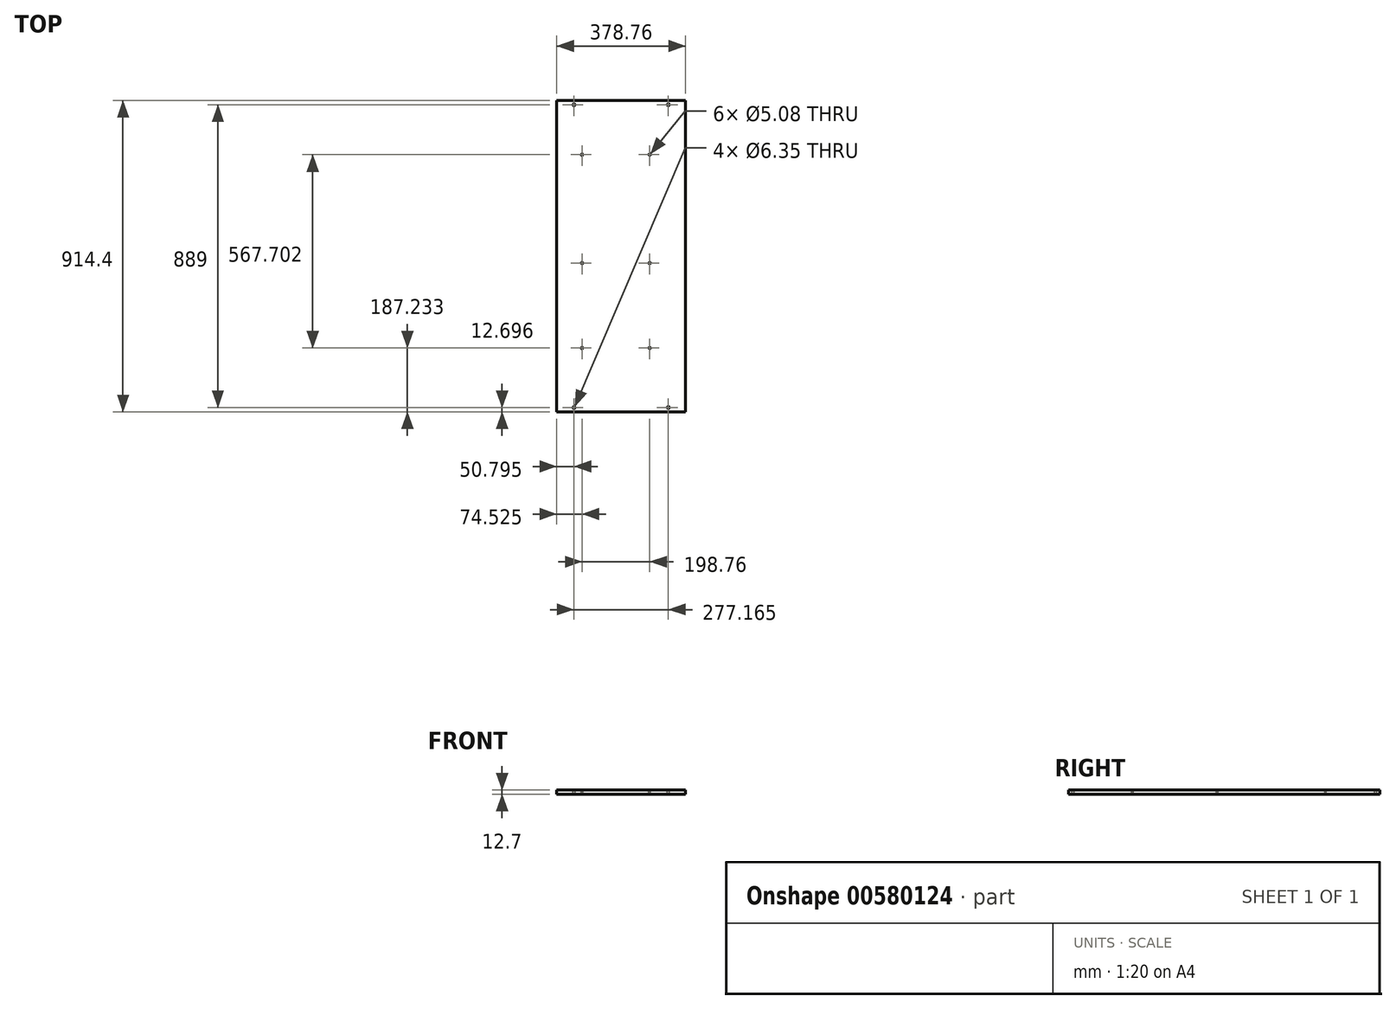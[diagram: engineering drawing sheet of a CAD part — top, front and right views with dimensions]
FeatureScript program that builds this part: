
annotation { "Feature Type Name" : "Feature", "Feature Type Description" : "" }
export const myFeature = defineFeature(function(context is Context, id is Id, definition is map)
    precondition{}
    {
        {
            var Q0;
            Q0=qCreatedBy(makeId("Top.planeOp"),FACE);
            var sketch = newSketch(context, id + "F0", { "sketchPlane" : qUnion([Q0])});
            skLineSegment(sketch, "E0.bottom", {"start": v(185.25, 527.23) * mm, "end": v(-193.51, 527.23) * mm});
            skLineSegment(sketch, "E0.top", {"start": v(185.25, -387.17) * mm, "end": v(-193.51, -387.17) * mm});
            skLineSegment(sketch, "E0.left", {"start": v(185.25, 527.23) * mm, "end": v(185.25, -387.17) * mm});
            skLineSegment(sketch, "E0.right", {"start": v(-193.51, 527.23) * mm, "end": v(-193.51, -387.17) * mm});
            skPoint(sketch, "E0.middle", {"position": v(-4.13, 70.03) * mm});
            skSolve(sketch);
        }
        {
            var Q0;
            Q0=qSketchRegion(id+"F0",true);
            extrude(context, id + "F1", {"entities" : qUnion([Q0]), "depth" : 12.7 * mm, "offsetDistance" : 25.4 * mm});
        }
        {
            var Q0;
            Q0=makeQuery(id+"F1.opExtrude","CAP_FACE",FACE,{"disambiguationData":[OSD([sQuery(id+"F0.wireOp",EDGE,"E0.bottom"),sQuery(id+"F0.wireOp",EDGE,"E0.top"),sQuery(id+"F0.wireOp",EDGE,"E0.left"),sQuery(id+"F0.wireOp",EDGE,"E0.right")])],"isStart":false});
            var sketch = newSketch(context, id + "F2", { "sketchPlane" : qUnion([Q0])});
            skCircle(sketch, "E1", {"center": v(-142.71, 514.53) * mm, "radius": 3.18 * mm});
            skCircle(sketch, "E2", {"center": v(134.45, 514.53) * mm, "radius": 3.18 * mm});
            skCircle(sketch, "E3", {"center": v(-142.71, -374.47) * mm, "radius": 3.17 * mm});
            skCircle(sketch, "E4", {"center": v(134.45, -374.47) * mm, "radius": 3.17 * mm});
            skLineSegment(sketch, "E5", {"start": v(-142.71, 514.53) * mm, "end": v(-142.71, 517.7) * mm});
            skLineSegment(sketch, "E6", {"start": v(-142.71, 517.7) * mm, "end": v(-142.71, 527.23) * mm});
            skLineSegment(sketch, "E7", {"start": v(134.45, 514.53) * mm, "end": v(134.45, 517.7) * mm});
            skLineSegment(sketch, "E8", {"start": v(134.45, 517.7) * mm, "end": v(134.45, 527.23) * mm});
            skLineSegment(sketch, "E9", {"start": v(134.45, -374.47) * mm, "end": v(134.45, -377.65) * mm});
            skLineSegment(sketch, "E10", {"start": v(134.45, -377.65) * mm, "end": v(134.45, -387.17) * mm});
            skLineSegment(sketch, "E11", {"start": v(-142.71, -374.47) * mm, "end": v(-142.71, -377.65) * mm});
            skLineSegment(sketch, "E12", {"start": v(-142.71, -377.65) * mm, "end": v(-142.71, -387.17) * mm});
            skSolve(sketch);
        }
        {
            var Q0;
            Q0=qSketchRegion(id+"F2",true);
            extrude(context, id + "F3", {"entities" : qUnion([Q0]), "operationType" : NewBodyOperationType.REMOVE, "endBound" : BoundingType.THROUGH_ALL, "oppositeDirection" : true, "depth" : 25.4 * mm, "offsetDistance" : 25.4 * mm});
        }
        {
            var Q0;
            Q0=makeQuery(id+"F1.opExtrude","CAP_FACE",FACE,{"disambiguationData":[OSD([sQuery(id+"F0.wireOp",EDGE,"E0.bottom"),sQuery(id+"F0.wireOp",EDGE,"E0.top"),sQuery(id+"F0.wireOp",EDGE,"E0.left"),sQuery(id+"F0.wireOp",EDGE,"E0.right")])],"isStart":false});
            var sketch = newSketch(context, id + "F4", { "sketchPlane" : qUnion([Q0])});
            skPoint(sketch, "E13", {"position": v(-118.98, -199.94) * mm});
            skPoint(sketch, "E14", {"position": v(-118.98, 49.68) * mm});
            skPoint(sketch, "E15", {"position": v(-118.98, 367.77) * mm});
            skPoint(sketch, "E16", {"position": v(79.77, 367.77) * mm});
            skPoint(sketch, "E17", {"position": v(79.77, 49.68) * mm});
            skPoint(sketch, "E18", {"position": v(79.77, -199.94) * mm});
            skPoint(sketch, "E19", {"position": v(-597.5, -357.88) * mm});
            skSolve(sketch);
        }
        {
            var Q0;
            Q0=sQuery(id+"F4.wireOp",VERTEX,"E14");
            var Q1;
            Q1=sQuery(id+"F4.wireOp",VERTEX,"E17");
            var Q2;
            Q2=sQuery(id+"F4.wireOp",VERTEX,"E15");
            var Q3;
            Q3=sQuery(id+"F4.wireOp",VERTEX,"E16");
            var Q4;
            Q4=sQuery(id+"F4.wireOp",VERTEX,"E13");
            var Q5;
            Q5=sQuery(id+"F4.wireOp",VERTEX,"E18");
            var Q6;
            Q6=makeQuery(id+"F1.opExtrude","SWEPT_BODY",BODY,{"disambiguationData":[OSD([sQuery(id+"F0.wireOp",EDGE,"E0.bottom"),sQuery(id+"F0.wireOp",EDGE,"E0.top"),sQuery(id+"F0.wireOp",EDGE,"E0.left"),sQuery(id+"F0.wireOp",EDGE,"E0.right")])]});
            hole(context, id + "F5", {"style" : HoleStyle.SIMPLE, "endStyle" : HoleEndStyle.THROUGH, "holeDiameter" : 5.08 * mm, "majorDiameter" : 6.35 * mm, "isTappedThrough" : true, "tappedDepth" : 12.7 * mm, "tapClearance" : 3, "locations" : qUnion([Q0, Q1, Q2, Q3, Q4, Q5]), "scope" : qUnion([Q6])});
        }
    });
